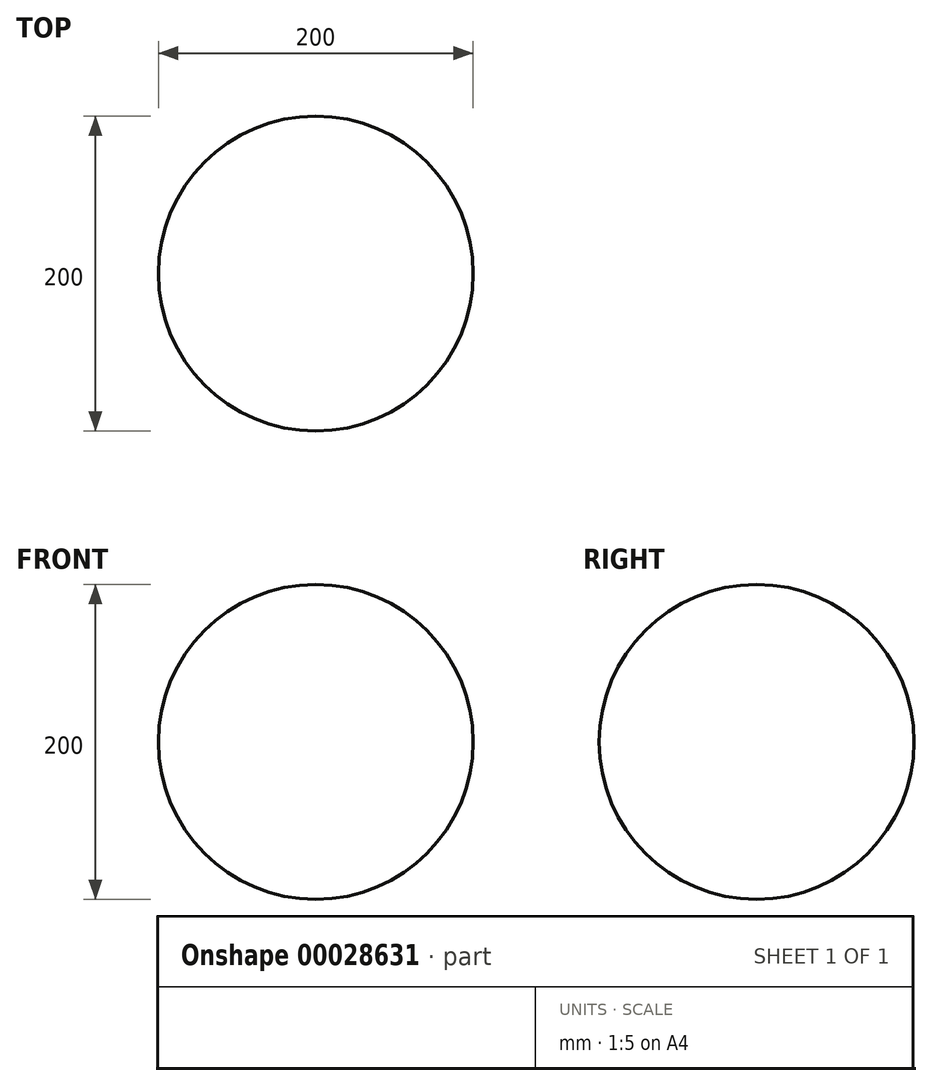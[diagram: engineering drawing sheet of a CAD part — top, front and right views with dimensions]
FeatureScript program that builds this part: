
annotation { "Feature Type Name" : "Feature", "Feature Type Description" : "" }
export const myFeature = defineFeature(function(context is Context, id is Id, definition is map)
    precondition{}
    {
        {
            var Q0;
            Q0=qCreatedBy(makeId("Front.planeOp"),FACE);
            var sketch = newSketch(context, id + "F0", { "sketchPlane" : qUnion([Q0])});
            skArc(sketch, "E0", {"start": v(0, 100) * mm, "mid": v(-100, 0) * mm, "end": v(0, -100) * mm});
            skLineSegment(sketch, "E1", {"start": v(0, 100) * mm, "end": v(0, -100) * mm});
            skSolve(sketch);
        }
        {
            var Q0;
            Q0 = qSketchRegion(id + "F0", true);
            var Q1;
            Q1=sQuery(id+"F0.wireOp",EDGE,"E1");
            revolve(context, id + "F1", {"surfaceOperationType" : NewSurfaceOperationType.NEW, "entities" : qUnion([Q0]), "axis" : qUnion([Q1]), "revolveType" : RevolveType.FULL});
        }
    });
